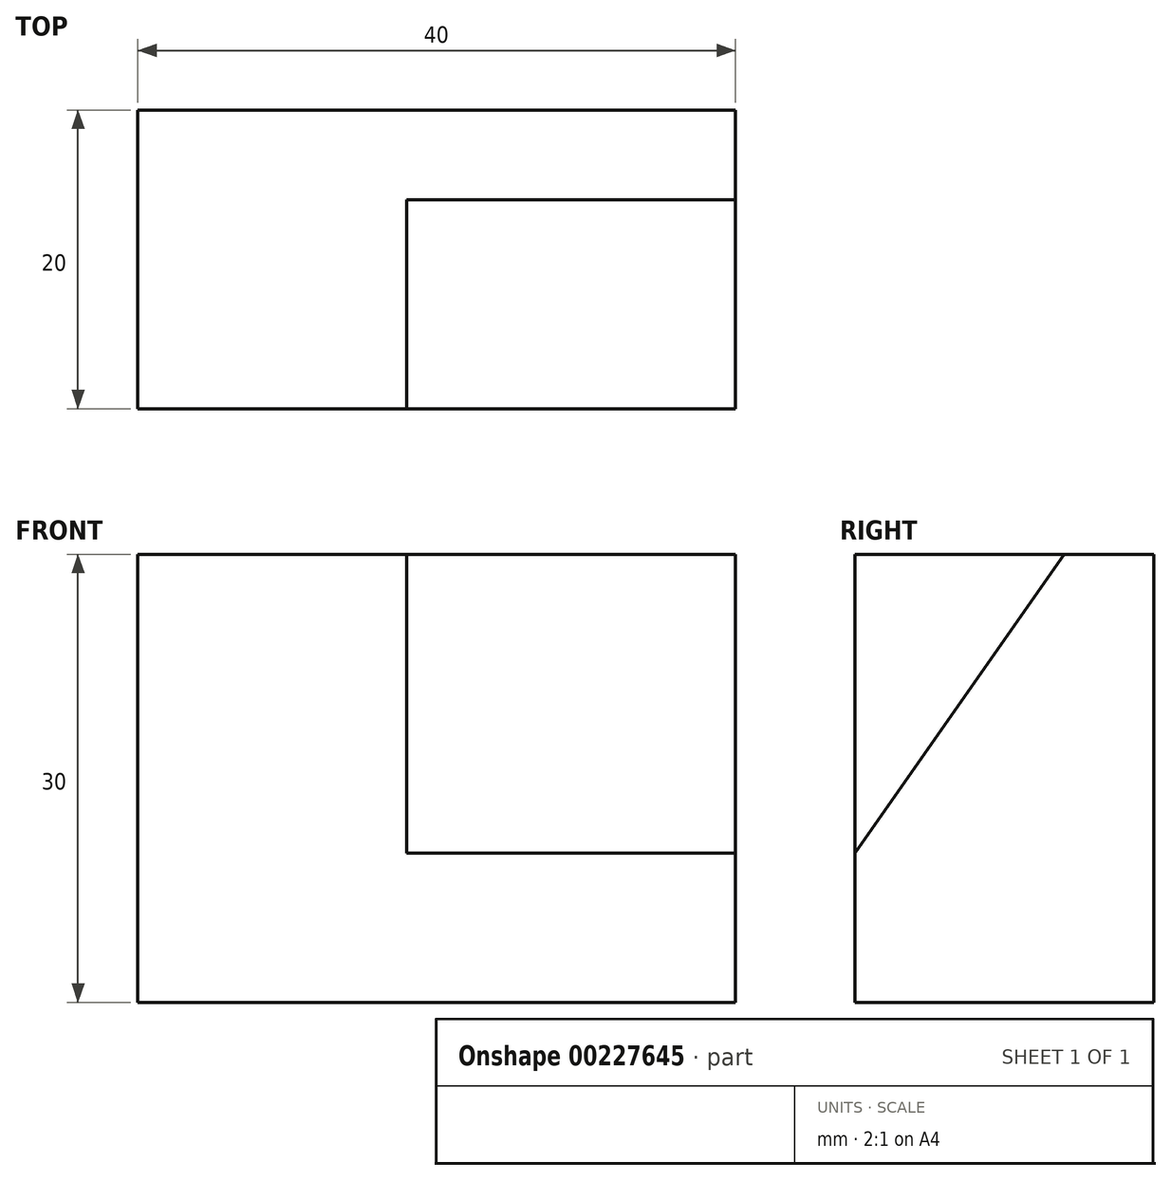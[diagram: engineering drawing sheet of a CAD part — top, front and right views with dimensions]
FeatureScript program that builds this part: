
annotation { "Feature Type Name" : "Feature", "Feature Type Description" : "" }
export const myFeature = defineFeature(function(context is Context, id is Id, definition is map)
    precondition{}
    {
        {
            var Q0;
            Q0=qCreatedBy(makeId("Front.planeOp"),FACE);
            var sketch = newSketch(context, id + "F0", { "sketchPlane" : qUnion([Q0])});
            skLineSegment(sketch, "E0.bottom", {"start": v(20, 15) * mm, "end": v(-20, 15) * mm});
            skLineSegment(sketch, "E0.top", {"start": v(20, -15) * mm, "end": v(-20, -15) * mm});
            skLineSegment(sketch, "E0.left", {"start": v(20, 15) * mm, "end": v(20, -15) * mm});
            skLineSegment(sketch, "E0.right", {"start": v(-20, 15) * mm, "end": v(-20, -15) * mm});
            skPoint(sketch, "E0.middle", {"position": v(0, 0) * mm});
            skSolve(sketch);
        }
        {
            var Q0;
            Q0=makeQuery(id+"F0.imprint","IMPRINT",FACE,{"disambiguationData":[TD([[makeQuery(id+"F0.imprint","IMPRINT",EDGE,{"derivedFrom":sQuery(id+"F0.wireOp",EDGE,"E0.bottom")}),1.0]])]});
            extrude(context, id + "F1", {"entities" : qUnion([Q0]), "depth" : 20 * mm});
        }
        {
            var Q0;
            Q0=makeQuery(id+"F1.opExtrude","SWEPT_FACE",FACE,{"disambiguationData":[OSD([sQuery(id+"F0.wireOp",EDGE,"E0.left")])]});
            var sketch = newSketch(context, id + "F2", { "sketchPlane" : qUnion([Q0])});
            skLineSegment(sketch, "E1.0", {"start": v(-20, 15) * mm, "end": v(-6, 15) * mm});
            skLineSegment(sketch, "E2.0", {"start": v(-20, 15) * mm, "end": v(-20, -5) * mm});
            skLineSegment(sketch, "E3", {"start": v(-6, 15) * mm, "end": v(-20, -5) * mm});
            skPoint(sketch, "E4.orphan", {"position": v(-20, -15) * mm});
            skPoint(sketch, "E5.orphan", {"position": v(0, 15) * mm});
            skSolve(sketch);
        }
        {
            var Q0;
            Q0 = qSketchRegion(id + "F2", true);
            extrude(context, id + "F3", {"entities" : qUnion([Q0]), "operationType" : NewBodyOperationType.REMOVE, "oppositeDirection" : true, "depth" : (40 - 18) * mm});
        }
    });
